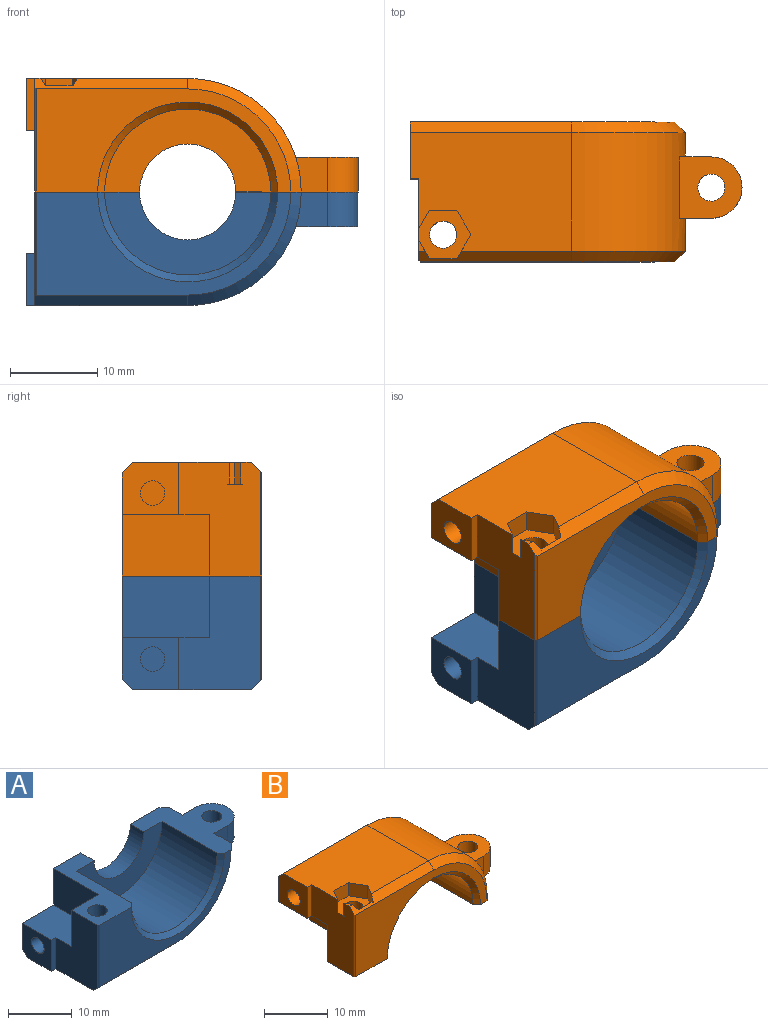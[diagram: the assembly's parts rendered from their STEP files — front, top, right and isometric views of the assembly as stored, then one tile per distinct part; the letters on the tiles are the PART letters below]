
ASSEMBLY  parts=2 mates=1
PART A: 29 faces, bbox 38x16x13 mm
  f0: cylinder r=13mm len=13.6mm, axis (0,-1,0), area 249.3mm2, adj f7,f8,f20,f21,f24,f26,f28
  f1: plane 7x6mm, normal (0,1,0), area 42mm2, adj f4,f16,f17,f22
  f2: plane 12x0.2mm, normal (-0.71,-0.71,0), area 3.4mm2, adj f3,f4,f11,f22
  f3: plane 17.5x1.2mm, normal (0,-0.71,-0.71), area 29.7mm2, adj f2,f8,f11,f21,f22
  f4: plane 16x12mm, normal (0,0,1), area 72.1mm2, adj f1,f2,f6,f9,f10,f11,f12,f15
  f5: plane 6.5x6mm, normal (-1,0,0), area 32.1mm2, adj f8,f9,f13,f17,f19,f23
  f6: plane 19x9.5mm, normal (0,-1,0), area 94.2mm2, adj f4,f7,f10,f15
  f7: plane 16x14mm, normal (0,0,1), area 98.9mm2, adj f0,f6,f9,f10,f11,f12,f15,f20
  f8: plane 18.5x13.6mm, normal (0,0,-1), area 235.8mm2, adj f0,f3,f5,f18,f19,f22,f23
  f9: plane 30.3x11.8mm, normal (0,1,0), area 231.1mm2, adj f4,f5,f7,f15,f16,f17,f19,f20
  f10: cylinder r=9.5mm len=19mm, axis (0,1,0), area 364.1mm2, adj f4,f6,f7,f12
  f11: plane 29.1x11.8mm, normal (0,-1,0), area 146.9mm2, adj f2,f3,f4,f7,f12,f21
  f12: cone r=9.5mm half-angle=45deg, axis (0,-1,0), area 35.2mm2, adj f4,f7,f10,f11
  f13: cylinder r=1.4mm len=5mm, axis (-1,0,0), area 44mm2, adj f5,f14
  f14: plane 2.8x2.8mm, normal (-1,0,0), area 6.2mm2, adj f13
  f15: cylinder r=5.5mm len=11mm, axis (0,-1,0), area 51.8mm2, adj f4,f6,f7,f9
  f16: plane 10x7mm, normal (-1,0,0), area 70mm2, adj f1,f4,f9,f17
  f17: plane 10x7mm, normal (0,0,1), area 66.5mm2, adj f1,f5,f9,f16,f22,f23
  f18: cylinder r=1.55mm len=13mm, axis (0,0,1), area 126.6mm2, adj f4,f8
  f19: plane 18.5x1.2mm, normal (0,0.71,-0.71), area 31.4mm2, adj f5,f8,f9,f20
  f20: cone r=13mm half-angle=45deg, axis (0,-1,0), area 33.1mm2, adj f0,f7,f9,f19
  f21: cone r=11.8mm half-angle=45deg, axis (0,1,0), area 33.1mm2, adj f0,f3,f7,f11
  f22: plane 13x9.3mm, normal (-1,0,0), area 95.9mm2, adj f1,f2,f3,f4,f8,f17,f23
  f23: plane 6x1mm, normal (0,-1,0), area 6mm2, adj f5,f8,f17,f22
  f24: plane 4x3.63mm, normal (0,-1,0), area 12.8mm2, adj f0,f7,f25,f28
  f25: cylinder r=3.5mm len=7mm, axis (0,0,1), area 44mm2, adj f7,f24,f26,f28
  f26: plane 4x3.63mm, normal (0,1,0), area 12.8mm2, adj f0,f7,f25,f28
  f27: cylinder r=1.55mm len=4mm, axis (0,0,1), area 39mm2, adj f7,f28
  f28: plane 7.13x7mm, normal (0,0,-1), area 37.1mm2, adj f0,f24,f25,f26,f27
PART B: 37 faces, bbox 38x16x13 mm
  f0: plane 1.24x0.72mm, normal (0,0,1), area 0.5mm2, adj f2,f4,f30
  f1: plane 18.5x13.6mm, normal (0,0,1), area 220mm2, adj f2,f4,f5,f6,f22,f24,f32,f33
  f2: plane 17.5x1.2mm, normal (0,-0.71,0.71), area 25.3mm2, adj f0,f1,f4,f9,f16,f21,f30,f31
  f3: cylinder r=1.55mm len=10.5mm, axis (0,0,1), area 102.3mm2, adj f11,f36
  f4: plane 13x9.3mm, normal (-1,0,0), area 92.6mm2, adj f0,f1,f2,f7,f8,f9,f11,f24
  f5: cylinder r=13mm len=13.6mm, axis (0,-1,0), area 249.3mm2, adj f1,f13,f21,f23,f25,f27,f29
  f6: plane 6.5x6mm, normal (-1,0,0), area 32.1mm2, adj f1,f7,f14,f18,f22,f24
  f7: plane 10x7mm, normal (0,0,-1), area 66.5mm2, adj f4,f6,f8,f10,f14,f24
  f8: plane 7x6mm, normal (0,1,0), area 42mm2, adj f4,f7,f10,f11
  f9: plane 12x0.2mm, normal (-0.71,-0.71,0), area 3.4mm2, adj f2,f4,f11,f16
  f10: plane 10x7mm, normal (-1,0,0), area 70mm2, adj f7,f8,f11,f14
  f11: plane 16x12mm, normal (0,0,-1), area 72.1mm2, adj f3,f4,f8,f9,f10,f12,f14,f15
  f12: plane 19x9.5mm, normal (0,-1,0), area 94.2mm2, adj f11,f13,f15,f20
  f13: plane 16x14mm, normal (0,0,-1), area 98.9mm2, adj f5,f12,f14,f15,f16,f17,f20,f21
  f14: plane 30.3x11.8mm, normal (0,1,0), area 231.1mm2, adj f6,f7,f10,f11,f13,f20,f22,f23
  f15: cylinder r=9.5mm len=19mm, axis (0,1,0), area 364.1mm2, adj f11,f12,f13,f17
  f16: plane 29.1x11.8mm, normal (0,-1,0), area 146.9mm2, adj f2,f9,f11,f13,f17,f21
  f17: cone r=9.5mm half-angle=45deg, axis (0,-1,0), area 35.2mm2, adj f11,f13,f15,f16
  f18: cylinder r=1.4mm len=5mm, axis (-1,0,0), area 44mm2, adj f6,f19
  f19: plane 2.8x2.8mm, normal (-1,0,0), area 6.2mm2, adj f18
  f20: cylinder r=5.5mm len=11mm, axis (0,-1,0), area 51.8mm2, adj f11,f12,f13,f14
  f21: cone r=11.8mm half-angle=45deg, axis (0,1,0), area 33.1mm2, adj f2,f5,f13,f16
  f22: plane 18.5x1.2mm, normal (0,0.71,0.71), area 31.4mm2, adj f1,f6,f14,f23
  f23: cone r=13mm half-angle=45deg, axis (0,-1,0), area 33.1mm2, adj f5,f13,f14,f22
  f24: plane 6x1mm, normal (0,-1,0), area 6mm2, adj f1,f4,f6,f7
  f25: plane 4x3.63mm, normal (0,1,0), area 12.8mm2, adj f5,f13,f26,f29
  f26: cylinder r=3.5mm len=7mm, axis (0,0,-1), area 44mm2, adj f13,f25,f27,f29
  f27: plane 4x3.63mm, normal (0,-1,0), area 12.8mm2, adj f5,f13,f26,f29
  f28: cylinder r=1.55mm len=4mm, axis (0,0,-1), area 39mm2, adj f13,f29
  f29: plane 7.13x7mm, normal (0,0,1), area 37.1mm2, adj f5,f25,f26,f27,f28
  f30: plane 2.5x2.1mm, normal (0.86,0.5,0), area 5.6mm2, adj f0,f2,f4,f31,f36
  f31: plane 3.18x1.66mm, normal (0,1,0), area 5.2mm2, adj f2,f30,f32,f36
  f32: plane 2.76x2.5mm, normal (-0.87,0.5,0), area 7.5mm2, adj f1,f2,f31,f33,f36
  f33: plane 2.75x2.5mm, normal (-0.86,-0.5,0), area 7.9mm2, adj f1,f32,f34,f36
  f34: plane 3.18x2.5mm, normal (0,-1,0), area 7.9mm2, adj f1,f33,f35,f36
  f35: plane 2.5x2.1mm, normal (0.87,-0.5,0), area 6.1mm2, adj f1,f4,f34,f36
  f36: plane 5.98x5.51mm, normal (0,0,1), area 18.4mm2, adj f3,f4,f30,f31,f32,f33,f34,f35
PLACE A t=(16.9,17.13,-3.51)mm
PLACE B t=(16.9,17.13,-3.51)mm
MATE fastened B.f3 <-> A.f18  axis (0,0,-1) through (2.2,7.23,-3.51)mm
